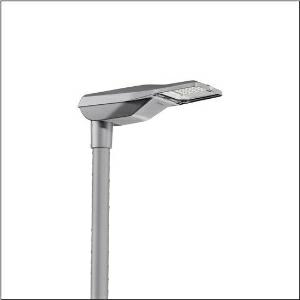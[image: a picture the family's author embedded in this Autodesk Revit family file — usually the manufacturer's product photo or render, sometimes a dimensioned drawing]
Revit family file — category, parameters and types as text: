
# Revit family: streetlight_sl_21_iq_micro___p0_5a_5xe1v31d08cb_9f45
name_source: partatom
category: Lighting Fixtures
units: mm (PartAtom-declared; Revit-internal decimal feet)

## family parameters
Cut with Voids When Loaded = No
Host = Face
Light Source = No
Part Type = Normal
Room Calculation Point = No
Round Connector Dimension = Use Diameter
Shared = No

## types (1)
- --- (1 x LED, 2780 lm, 19.4 W, 3000K)
    Apparent Load = 19 VA
    CIE Flux Codes = 37 73 96 100 100
    Color Rendering = 70
    Color Temperature = 3000K
    Default Elevation = 1800 mm
    Description = Streetlight SL 21 iQ micro, mast luminaire, primary light control with lens, of PMMA, primary optical cover: cover, of toughened safety glass, transparent, light distribution: P0.5a, light emission: direct distribution, primary light characteristic: asymmetric, installation type: post-top, side-entry, LED, High Power LED, rated luminous flux: 2.780lm, luminous efficacy: 143lm/W, light colour: 730, colour temperature: 3000K, control gear: iQ-Comfort, control: pre-setting: linear dimming characteristic, Auto-Match, Temp-Guard, Lumen-Switch, Night-Set, Smart-Wire, Light-Fading, Desk-Remote (wireless, voltage-free reading and setting of iQ features in the workshop via application-optimized NFC function/RFID function), optimised constant luminous flux control (CLO 2.0), mains connection: 220..240V, AC, 50/60Hz, start of lifetime: 19W, end of service life: 20W, reduction: 10W, luminaire housing, of diecast aluminium, powder-coated, Siteco® metallic grey (DB 702S), corrosivity category C5 mid according to DIN EN ISO 12944, please order mast flange separately, inclination adjustable: 0°, 5°, 10°, 15°, sealing non-destructively replaceable, multi-level sealing system, length: 528mm, width: 235mm, height: 110mm, mast flange for spigot size: 42mm (side-entry): 5XC10008XM4, 60/48mm (side-entry/post-top): 5XC10108XM2, 76/60mm (side-entry/post-top): 5XC10108XM1, protection rating (complete): IP66, insulation class (complete): insulation class II (safety insulation), certification: CE, ENEC, ENEC+, VDE, impact resistance: IK10, permissible operating ambient temperature for outdoor applications: -40..+50°C, standard-compliant lighting for roads and squares, packaging unit: 1 piece

Light Distribution: P0.5a
    Height = 110 mm
    Lamp = 1 x LED
    Lamp Light Flux = 2780 lm
    Lamp Power = 19.4 W
    Lamp count = 1
    Length = 528 mm
    Luminous efficacy = 143 lm/W
    Manufacturer = Siteco
    ModVariant = No
    Model = 5XE1V31D08CB
    Number of Poles = 1
    OnlyDefault = Yes
    Power Factor = 1
    Product Name = Streetlight SL 21 iQ micro | P0.5a
    Product group = mast luminaire | pylon top
    ProductGroupID = 6100
    Protection Class = Protection class II
    Protection Degree = IP 66
    RLX_Detail_Level = 1
    RLX_Emergency_Light_Flux = 0 lm
    RLX_Emergency_Type = 0
    RLX_Emergency_Type_DB = No
    RlxData = <blob elided: 98541 chars, md5=0015ba86>
    Socket = socket
    Standby Power = 0 W
    System Light Flux = 2780 lm
    System Power = 19 W
    Type Comments = factory setting: luminous flux: 100 % | dim-lin: 254 | 387 mA
    Type Image = l_1006881.jpg
    URL = http://relux.com
    VarID = @adj_091853
    Voltage = 0 V
    Weight = 0.00 kg
    Width = 235 mm

## geometry (parser evidence)
native form markers: Blend x4, Sweep x9
no freeform markers — native parametric forms only
